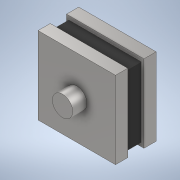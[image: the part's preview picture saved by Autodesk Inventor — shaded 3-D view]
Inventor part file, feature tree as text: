
AUTODESK INVENTOR PART (.ipt)
format: ipt  version: 2022 (Build 260153070, 153G)  size: 125,440 bytes
history: native  units: mm
features: extrude x4, sketch x4
ambient origin geometry x8: Origin, YZ Plane, XZ Plane, XY Plane, X Axis, Y Axis, Z Axis, Center Point
bodies: Solid1 (feature_tree)
feature tree (8):
  extrude  "Extrusion1"  Depth=38.1mm
  extrude  "Extrusion2"  Depth=8.0mm TaperAngle=0.0deg
  extrude  "Extrusion3"  Depth=10.0mm
  extrude  "Extrusion4"  Depth=7.0mm
  sketch  "Sketch1"  dims[d0=38.1mm d1=38.1mm]
  sketch  "Sketch2"  dims[d2=6.0mm d3=0.0mm d4=8.0mm d5=0.0mm]
  sketch  "Sketch3"  dims[d6=6.0mm d7=0.0mm d8=10.0mm]
  sketch  "Sketch4"  dims[d9=19.05mm d10=19.05mm d11=7.0mm d12=0.0mm]
